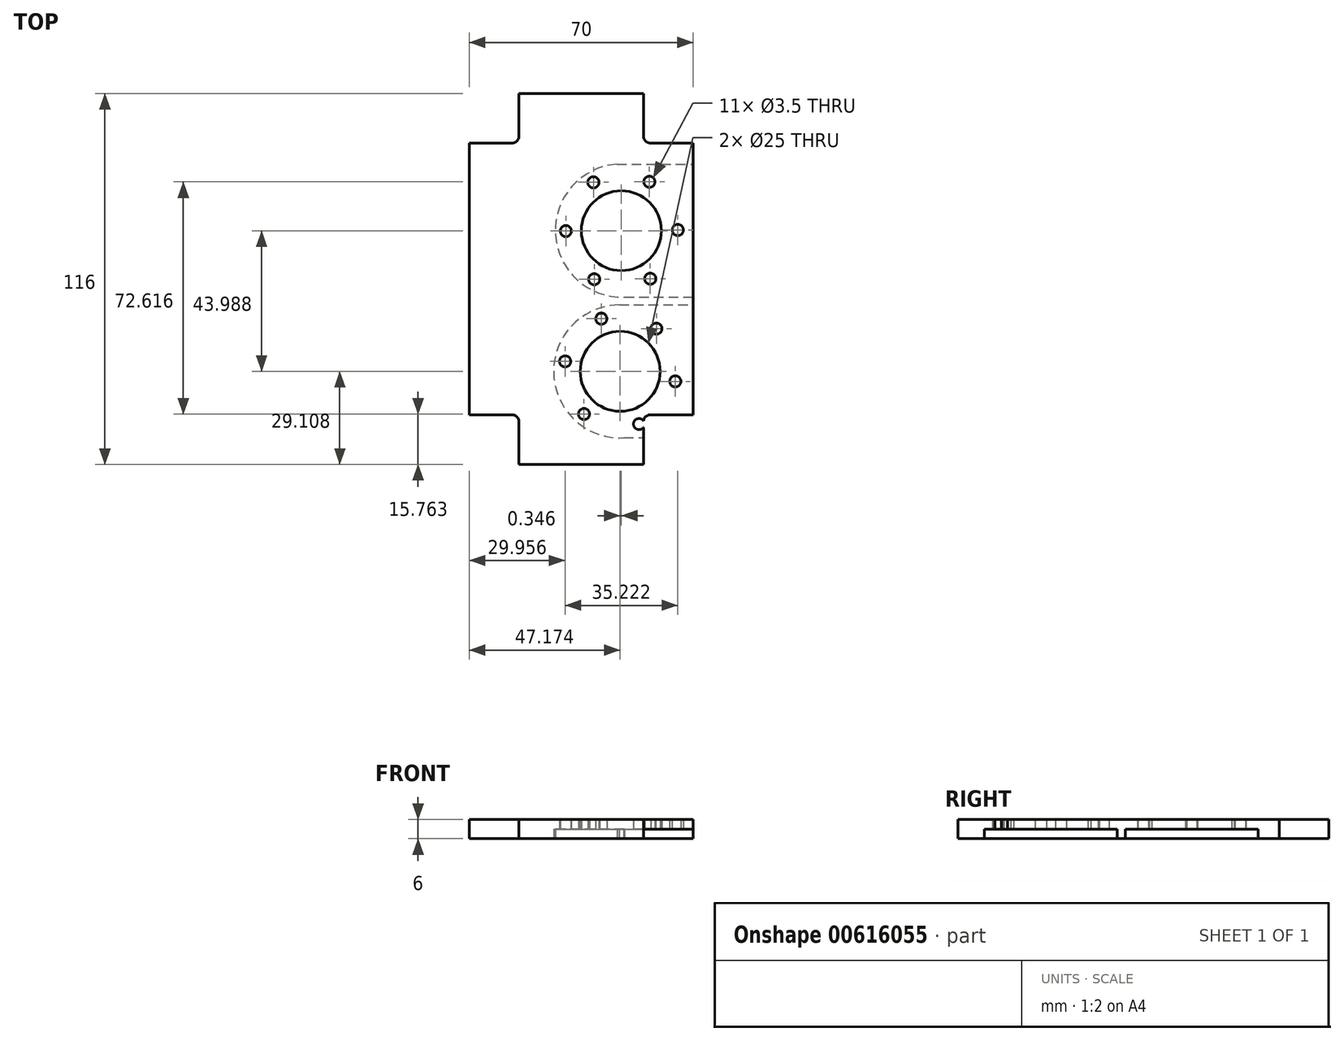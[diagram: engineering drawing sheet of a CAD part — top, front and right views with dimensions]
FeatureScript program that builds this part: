
annotation { "Feature Type Name" : "Feature", "Feature Type Description" : "" }
export const myFeature = defineFeature(function(context is Context, id is Id, definition is map)
    precondition{}
    {
        {
            var Q0;
            Q0=qCreatedBy(makeId("Top.planeOp"),FACE);
            var sketch = newSketch(context, id + "F0", { "sketchPlane" : qUnion([Q0])});
            skLineSegment(sketch, "E0.top", {"start": v(0, -15.5) * mm, "end": v(15.5, -15.5) * mm});
            skLineSegment(sketch, "E0.right", {"start": v(15.5, 0) * mm, "end": v(15.5, -15.5) * mm});
            skLineSegment(sketch, "E1.top", {"start": v(70, -15.5) * mm, "end": v(54.5, -15.5) * mm});
            skLineSegment(sketch, "E1.right", {"start": v(54.5, 0) * mm, "end": v(54.5, -15.5) * mm});
            skLineSegment(sketch, "E2", {"start": v(15.5, 0) * mm, "end": v(54.5, 0) * mm});
            skLineSegment(sketch, "E3.top", {"start": v(0, -100.5) * mm, "end": v(15.5, -100.5) * mm});
            skLineSegment(sketch, "E3.right", {"start": v(15.5, -116) * mm, "end": v(15.5, -100.5) * mm});
            skLineSegment(sketch, "E4.top", {"start": v(70, -100.5) * mm, "end": v(54.5, -100.5) * mm});
            skLineSegment(sketch, "E4.right", {"start": v(54.5, -116) * mm, "end": v(54.5, -100.5) * mm});
            skLineSegment(sketch, "E5", {"start": v(70, -15.5) * mm, "end": v(70, -100.5) * mm});
            skLineSegment(sketch, "E6", {"start": v(54.5, -116) * mm, "end": v(15.5, -116) * mm});
            skLineSegment(sketch, "E7", {"start": v(0, -100.5) * mm, "end": v(0, -15.5) * mm});
            skSolve(sketch);
        }
        {
            var Q0;
            Q0 = qSketchRegion(id + "F0", true);
            extrude(context, id + "F1", {"entities" : qUnion([Q0]), "depth" : 6 * mm, "offsetDistance" : 25 * mm});
        }
        {
            var Q0;
            Q0=makeQuery(id+"F1.opExtrude","CAP_FACE",FACE,{"disambiguationData":[OSD([sQuery(id+"F0.wireOp",EDGE,"E0.top"),sQuery(id+"F0.wireOp",EDGE,"E0.right"),sQuery(id+"F0.wireOp",EDGE,"E1.top"),sQuery(id+"F0.wireOp",EDGE,"E1.right"),sQuery(id+"F0.wireOp",EDGE,"E2"),sQuery(id+"F0.wireOp",EDGE,"E3.top"),sQuery(id+"F0.wireOp",EDGE,"E3.right"),sQuery(id+"F0.wireOp",EDGE,"E4.top"),sQuery(id+"F0.wireOp",EDGE,"E4.right"),sQuery(id+"F0.wireOp",EDGE,"E5"),sQuery(id+"F0.wireOp",EDGE,"E6"),sQuery(id+"F0.wireOp",EDGE,"E7")])],"isStart":true});
            var sketch = newSketch(context, id + "F2", { "sketchPlane" : qUnion([Q0])});
            skArc(sketch, "E8", {"start": v(48.3, 107.66) * mm, "mid": v(26.39, 87.61) * mm, "end": v(46.86, 66.1) * mm});
            skArc(sketch, "E9", {"start": v(48.5, 63.64) * mm, "mid": v(26.91, 44.02) * mm, "end": v(46.17, 22.1) * mm});
            skLineSegment(sketch, "E10", {"start": v(46.04, 107.66) * mm, "end": v(70, 107.66) * mm});
            skLineSegment(sketch, "E11", {"start": v(46.86, 66.1) * mm, "end": v(70, 66.1) * mm});
            skLineSegment(sketch, "E12", {"start": v(46.86, 63.64) * mm, "end": v(70, 63.64) * mm});
            skLineSegment(sketch, "E13", {"start": v(46.17, 22.1) * mm, "end": v(70, 22.1) * mm});
            skSolve(sketch);
        }
        {
            var Q0;
            Q0 = qSketchRegion(id + "F2", true);
            var Q1;
            {var subQ6=sQuery(id+"F2.wireOp",EDGE,"E11");Q1=makeQuery(id+"F2.imprint","IMPRINT",FACE,{"disambiguationData":[TD([[makeQuery(id+"F2.imprint","IMPRINT",EDGE,{"derivedFrom":subQ6}),1.0]])]});}
            var Q2;
            {var subQ0=sQuery(id+"F2.wireOp",EDGE,"E13");Q2=makeQuery(id+"F2.imprint","IMPRINT",FACE,{"disambiguationData":[TD([[makeQuery(id+"F2.imprint","IMPRINT",EDGE,{"derivedFrom":subQ0}),1.0]])]});}
            extrude(context, id + "F3", {"entities" : qUnion([Q0, Q1, Q2]), "operationType" : NewBodyOperationType.REMOVE, "oppositeDirection" : true, "depth" : 3 * mm, "offsetDistance" : 25 * mm});
        }
        {
            var Q0;
            Q0=makeQuery(id+"F3.boolean.opBoolean","COPY",FACE,{"derivedFrom":makeQuery(id+"F3.opExtrude","CAP_FACE",FACE,{"disambiguationData":[OSD([sQuery(id+"F0.wireOp",EDGE,"E5"),sQuery(id+"F2.wireOp",EDGE,"E8"),sQuery(id+"F2.wireOp",EDGE,"E10"),sQuery(id+"F2.wireOp",EDGE,"E11")])],"isStart":false})});
            var sketch = newSketch(context, id + "F4", { "sketchPlane" : qUnion([Q0])});
            skCircle(sketch, "E14", {"center": v(47.17, 86.9) * mm, "radius": 12.5 * mm});
            skCircle(sketch, "E15", {"center": v(47.52, 42.9) * mm, "radius": 12.5 * mm});
            skCircle(sketch, "E16", {"center": v(47.17, 86.9) * mm, "radius": 17.5 * mm, "construction": true});
            skSolve(sketch);
        }
        {
            var Q0;
            Q0=makeQuery(id+"F4.imprint","IMPRINT",FACE,{"disambiguationData":[TD([[makeQuery(id+"F4.imprint","IMPRINT",EDGE,{"derivedFrom":sQuery(id+"F4.wireOp",EDGE,"E15")}),1.0]])]});
            var Q1;
            Q1=makeQuery(id+"F4.imprint","IMPRINT",FACE,{"disambiguationData":[TD([[makeQuery(id+"F4.imprint","IMPRINT",EDGE,{"derivedFrom":sQuery(id+"F4.wireOp",EDGE,"E14")}),1.0]])]});
            extrude(context, id + "F5", {"entities" : qUnion([Q0, Q1]), "operationType" : NewBodyOperationType.REMOVE, "oppositeDirection" : true, "depth" : 25 * mm, "offsetDistance" : 25 * mm});
        }
        {
            var Q0;
            Q0=makeQuery(id+"F3.boolean.opBoolean","COPY",FACE,{"derivedFrom":makeQuery(id+"F3.opExtrude","CAP_FACE",FACE,{"disambiguationData":[OSD([sQuery(id+"F0.wireOp",EDGE,"E5"),sQuery(id+"F2.wireOp",EDGE,"E9"),sQuery(id+"F2.wireOp",EDGE,"E12"),sQuery(id+"F2.wireOp",EDGE,"E13")])],"isStart":false})});
            var sketch = newSketch(context, id + "F6", { "sketchPlane" : qUnion([Q0])});
            skCircle(sketch, "E17", {"center": v(47.68, 42.85) * mm, "radius": 17.5 * mm, "construction": true});
            skCircle(sketch, "E18", {"center": v(39.07, 58.09) * mm, "radius": 1.75 * mm});
            skCircle(sketch, "E19.1.0", {"center": v(30.18, 43.01) * mm, "radius": 1.75 * mm});
            skCircle(sketch, "E19.2.0", {"center": v(38.8, 27.78) * mm, "radius": 1.75 * mm});
            skCircle(sketch, "E19.3.0", {"center": v(56.3, 27.62) * mm, "radius": 1.75 * mm});
            skCircle(sketch, "E19.4.0", {"center": v(65.18, 42.7) * mm, "radius": 1.75 * mm});
            skCircle(sketch, "E19.5.0", {"center": v(56.56, 57.93) * mm, "radius": 1.75 * mm});
            skSolve(sketch);
        }
        {
            var Q0;
            Q0 = qSketchRegion(id + "F6", true);
            extrude(context, id + "F7", {"entities" : qUnion([Q0]), "operationType" : NewBodyOperationType.REMOVE, "oppositeDirection" : true, "depth" : 25 * mm, "offsetDistance" : 25 * mm});
        }
        {
            var Q0;
            Q0=makeQuery(id+"F3.boolean.opBoolean","COPY",FACE,{"derivedFrom":makeQuery(id+"F3.opExtrude","CAP_FACE",FACE,{"disambiguationData":[OSD([sQuery(id+"F0.wireOp",EDGE,"E5"),sQuery(id+"F2.wireOp",EDGE,"E8"),sQuery(id+"F2.wireOp",EDGE,"E10"),sQuery(id+"F2.wireOp",EDGE,"E11")])],"isStart":false})});
            var sketch = newSketch(context, id + "F8", { "sketchPlane" : qUnion([Q0])});
            skCircle(sketch, "E20", {"center": v(47.17, 86.9) * mm, "radius": 17.5 * mm, "construction": true});
            skCircle(sketch, "E21", {"center": v(35.85, 100.24) * mm, "radius": 1.75 * mm});
            skCircle(sketch, "E22.1.0", {"center": v(29.96, 83.76) * mm, "radius": 1.75 * mm});
            skCircle(sketch, "E22.2.0", {"center": v(41.28, 70.42) * mm, "radius": 1.75 * mm});
            skCircle(sketch, "E22.3.0", {"center": v(58.5, 73.55) * mm, "radius": 1.75 * mm});
            skCircle(sketch, "E22.4.0", {"center": v(64.4, 90.02) * mm, "radius": 1.75 * mm});
            skCircle(sketch, "E22.5.0", {"center": v(53.07, 103.37) * mm, "radius": 1.75 * mm});
            skSolve(sketch);
        }
        {
            var Q0;
            Q0 = qSketchRegion(id + "F8", true);
            extrude(context, id + "F9", {"entities" : qUnion([Q0]), "operationType" : NewBodyOperationType.REMOVE, "oppositeDirection" : true, "depth" : 25 * mm, "offsetDistance" : 25 * mm});
        }
        {
            var Q0;
            Q0=makeQuery(id+"F1.opExtrude","SWEPT_EDGE",EDGE,{"disambiguationData":[OSD([sQuery(id+"F0.wireOp",EDGE,"E3.top"),sQuery(id+"F0.wireOp",EDGE,"E3.right")])]});
            var Q1;
            Q1=makeQuery(id+"F1.opExtrude","SWEPT_EDGE",EDGE,{"disambiguationData":[OSD([sQuery(id+"F0.wireOp",EDGE,"E4.top"),sQuery(id+"F0.wireOp",EDGE,"E4.right")])]});
            fillet(context, id + "F10", {"entities" : qUnion([Q0, Q1]), "radius" : 2 * mm, "tangentPropagation" : true, "allowEdgeOverflow" : false});
        }
        {
            var Q0;
            Q0=makeQuery(id+"F1.opExtrude","SWEPT_EDGE",EDGE,{"disambiguationData":[OSD([sQuery(id+"F0.wireOp",EDGE,"E1.top"),sQuery(id+"F0.wireOp",EDGE,"E1.right")])]});
            var Q1;
            Q1=makeQuery(id+"F1.opExtrude","SWEPT_EDGE",EDGE,{"disambiguationData":[OSD([sQuery(id+"F0.wireOp",EDGE,"E0.top"),sQuery(id+"F0.wireOp",EDGE,"E0.right")])]});
            fillet(context, id + "F11", {"entities" : qUnion([Q0, Q1]), "radius" : 2 * mm, "tangentPropagation" : true, "allowEdgeOverflow" : false});
        }
    });
